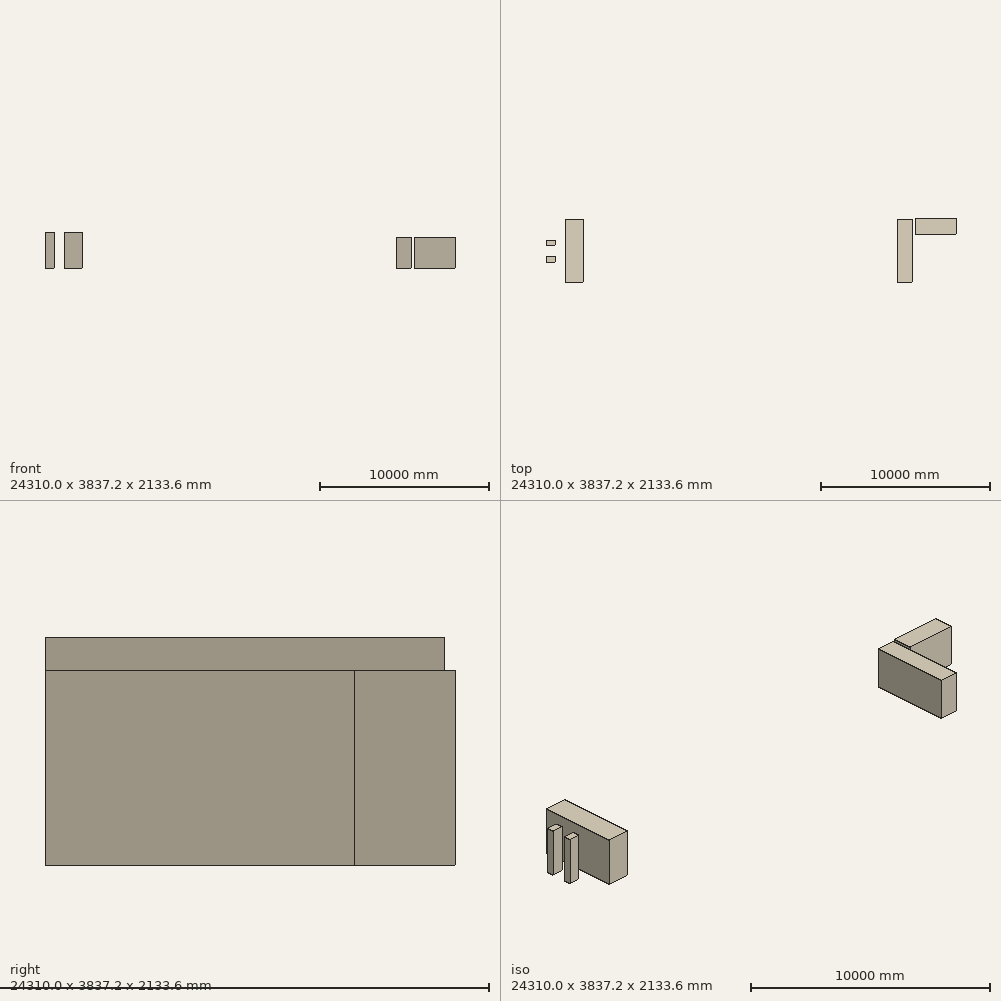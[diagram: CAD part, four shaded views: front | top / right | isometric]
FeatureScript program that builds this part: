
annotation { "Feature Type Name" : "Feature", "Feature Type Description" : "" }
export const myFeature = defineFeature(function(context is Context, id is Id, definition is map)
    precondition{}
    {
        {
            var Q0;
            Q0=qCreatedBy(makeId("Top.planeOp"),FACE);
            var sketch = newSketch(context, id + "F0", { "sketchPlane" : qUnion([Q0])});
            skLineSegment(sketch, "E0.bottom", {"start": v(493.4, -1960.48) * mm, "end": v(-406.6, -1960.48) * mm});
            skLineSegment(sketch, "E0.top", {"start": v(493.4, 1769.84) * mm, "end": v(-406.6, 1769.84) * mm});
            skLineSegment(sketch, "E0.left", {"start": v(493.4, -1960.48) * mm, "end": v(493.4, 1769.84) * mm});
            skLineSegment(sketch, "E0.right", {"start": v(-406.6, -1960.48) * mm, "end": v(-406.6, 1769.84) * mm});
            skPoint(sketch, "E0.middle", {"position": v(43.4, -95.32) * mm});
            skLineSegment(sketch, "E1.bottom", {"start": v(643.4, 934.68) * mm, "end": v(3093.4, 934.68) * mm});
            skLineSegment(sketch, "E1.top", {"start": v(643.4, 1876.68) * mm, "end": v(3093.4, 1876.68) * mm});
            skLineSegment(sketch, "E1.left", {"start": v(643.4, 934.68) * mm, "end": v(643.4, 1876.68) * mm});
            skLineSegment(sketch, "E1.right", {"start": v(3093.4, 934.68) * mm, "end": v(3093.4, 1876.68) * mm});
            skPoint(sketch, "E1.middle", {"position": v(1868.4, 1405.68) * mm});
            skLineSegment(sketch, "E2.bottom", {"start": v(2345.4, -45.32) * mm, "end": v(1845.4, -45.32) * mm});
            skLineSegment(sketch, "E2.top", {"start": v(2345.4, 454.68) * mm, "end": v(1845.4, 454.68) * mm});
            skLineSegment(sketch, "E2.left", {"start": v(2345.4, -45.32) * mm, "end": v(2345.4, 454.68) * mm});
            skLineSegment(sketch, "E2.right", {"start": v(1845.4, -45.32) * mm, "end": v(1845.4, 454.68) * mm});
            skPoint(sketch, "E2.middle", {"position": v(2095.4, 204.68) * mm});
            skLineSegment(sketch, "E3.bottom", {"start": v(2577.9, -1497.82) * mm, "end": v(1072.9, -1497.82) * mm});
            skLineSegment(sketch, "E3.top", {"start": v(2577.9, -1372.82) * mm, "end": v(1072.9, -1372.82) * mm});
            skLineSegment(sketch, "E3.left", {"start": v(2577.9, -1497.82) * mm, "end": v(2577.9, -1372.82) * mm});
            skLineSegment(sketch, "E3.right", {"start": v(1072.9, -1497.82) * mm, "end": v(1072.9, -1372.82) * mm});
            skPoint(sketch, "E3.middle", {"position": v(1825.4, -1435.32) * mm});
            skLineSegment(sketch, "E4.bottom", {"start": v(2590.38, 632.18) * mm, "end": v(1060.43, 632.18) * mm});
            skLineSegment(sketch, "E4.top", {"start": v(2590.38, 757.18) * mm, "end": v(1060.43, 757.18) * mm});
            skLineSegment(sketch, "E4.left", {"start": v(2590.38, 632.18) * mm, "end": v(2590.38, 757.18) * mm});
            skLineSegment(sketch, "E4.right", {"start": v(1060.43, 632.18) * mm, "end": v(1060.43, 757.18) * mm});
            skPoint(sketch, "E4.middle", {"position": v(1825.4, 694.68) * mm});
            skLineSegment(sketch, "E5.bottom", {"start": v(-19011.6, -1960.32) * mm, "end": v(-20081.6, -1960.32) * mm});
            skLineSegment(sketch, "E5.top", {"start": v(-19011.6, 1769.68) * mm, "end": v(-20081.6, 1769.68) * mm});
            skLineSegment(sketch, "E5.left", {"start": v(-19011.6, -1960.32) * mm, "end": v(-19011.6, 1769.68) * mm});
            skLineSegment(sketch, "E5.right", {"start": v(-20081.6, -1960.32) * mm, "end": v(-20081.6, 1769.68) * mm});
            skPoint(sketch, "E5.middle", {"position": v(-19546.6, -95.32) * mm});
            skLineSegment(sketch, "E6.bottom", {"start": v(-20696.6, 234.68) * mm, "end": v(-21216.6, 234.68) * mm});
            skLineSegment(sketch, "E6.top", {"start": v(-20696.6, 574.68) * mm, "end": v(-21216.6, 574.68) * mm});
            skLineSegment(sketch, "E6.left", {"start": v(-20696.6, 234.68) * mm, "end": v(-20696.6, 574.68) * mm});
            skLineSegment(sketch, "E6.right", {"start": v(-21216.6, 234.68) * mm, "end": v(-21216.6, 574.68) * mm});
            skPoint(sketch, "E6.middle", {"position": v(-20956.6, 404.68) * mm});
            skLineSegment(sketch, "E7.bottom", {"start": v(-20696.6, -765.32) * mm, "end": v(-21216.6, -765.32) * mm});
            skLineSegment(sketch, "E7.top", {"start": v(-20696.6, -425.32) * mm, "end": v(-21216.6, -425.32) * mm});
            skLineSegment(sketch, "E7.left", {"start": v(-20696.6, -765.32) * mm, "end": v(-20696.6, -425.32) * mm});
            skLineSegment(sketch, "E7.right", {"start": v(-21216.6, -765.32) * mm, "end": v(-21216.6, -425.32) * mm});
            skPoint(sketch, "E7.middle", {"position": v(-20956.6, -595.32) * mm});
            skPoint(sketch, "E8", {"position": v(-20956.6, -425.32) * mm});
            skLineSegment(sketch, "E9", {"start": v(43.4, -95.32) * mm, "end": v(-19546.6, -95.32) * mm});
            skSolve(sketch);
        }
        {
            var Q0;
            {var subQ3=sQuery(id+"F0.wireOp",EDGE,"E5.bottom");Q0=makeQuery(id+"F0.imprint","IMPRINT",FACE,{"disambiguationData":[TD([[makeQuery(id+"F0.imprint","IMPRINT",EDGE,{"derivedFrom":subQ3}),-1.0]])]});}
            var Q1;
            Q1=makeQuery(id+"F0.imprint","IMPRINT",FACE,{"disambiguationData":[TD([[makeQuery(id+"F0.imprint","IMPRINT",EDGE,{"derivedFrom":sQuery(id+"F0.wireOp",EDGE,"E6.bottom")}),-1.0]])]});
            var Q2;
            Q2=makeQuery(id+"F0.imprint","IMPRINT",FACE,{"disambiguationData":[TD([[makeQuery(id+"F0.imprint","IMPRINT",EDGE,{"derivedFrom":sQuery(id+"F0.wireOp",EDGE,"E7.bottom")}),-1.0]])]});
            extrude(context, id + "F1", {"entities" : qUnion([Q0, Q1, Q2]), "depth" : 2133.6 * mm});
        }
        {
            var Q0;
            {var subQ1=sQuery(id+"F0.wireOp",EDGE,"E0.bottom");Q0=makeQuery(id+"F0.imprint","IMPRINT",FACE,{"disambiguationData":[TD([[makeQuery(id+"F0.imprint","IMPRINT",EDGE,{"derivedFrom":subQ1}),-1.0]])]});}
            var Q1;
            Q1=makeQuery(id+"F0.imprint","IMPRINT",FACE,{"disambiguationData":[TD([[makeQuery(id+"F0.imprint","IMPRINT",EDGE,{"derivedFrom":sQuery(id+"F0.wireOp",EDGE,"E1.bottom")}),1.0]])]});
            extrude(context, id + "F2", {"entities" : qUnion([Q0, Q1]), "depth" : 1828.8 * mm});
        }
    });
